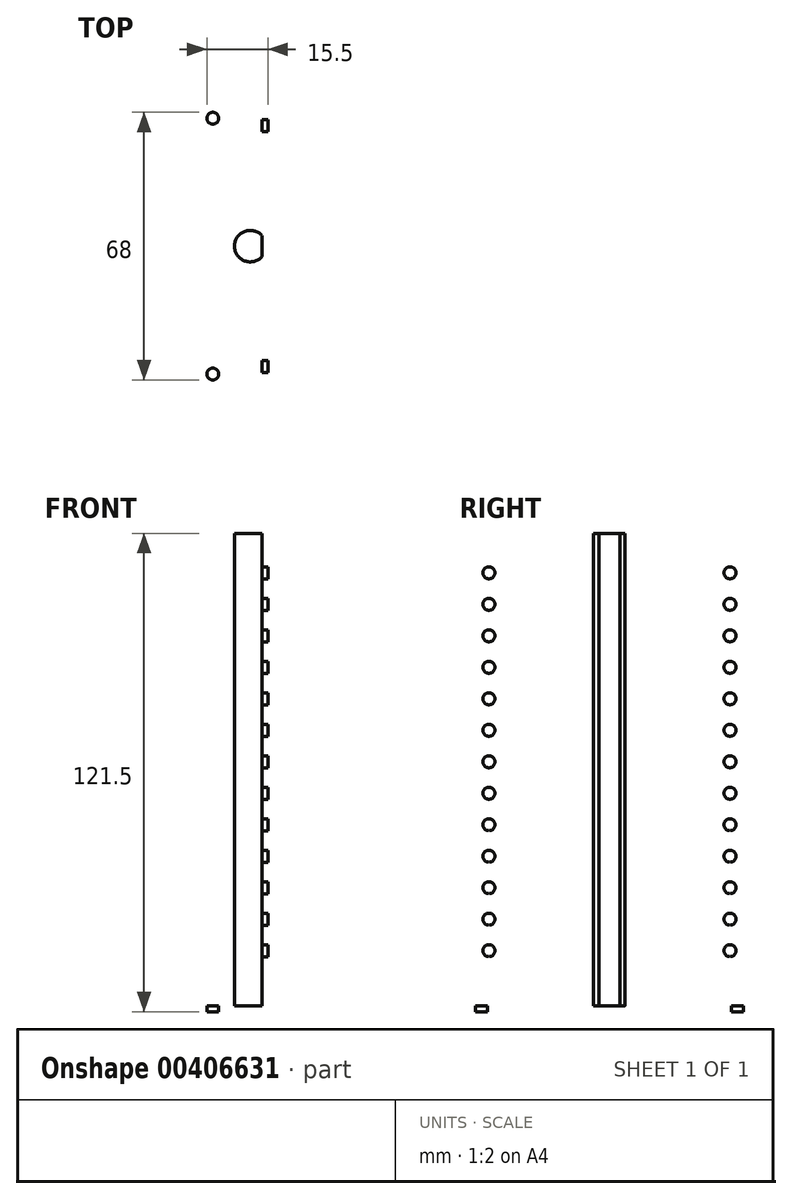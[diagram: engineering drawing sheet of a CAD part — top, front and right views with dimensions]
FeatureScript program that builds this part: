
annotation { "Feature Type Name" : "Feature", "Feature Type Description" : "" }
export const myFeature = defineFeature(function(context is Context, id is Id, definition is map)
    precondition{}
    {
        {
            var Q0;
            Q0=qCreatedBy(makeId("Top.planeOp"),FACE);
            var sketch = newSketch(context, id + "F0", { "sketchPlane" : qUnion([Q0])});
            skLineSegment(sketch, "E0.bottom", {"start": v(12.5, -37.5) * mm, "end": v(-12.5, -37.5) * mm});
            skLineSegment(sketch, "E0.top", {"start": v(12.5, 37.5) * mm, "end": v(-12.5, 37.5) * mm});
            skLineSegment(sketch, "E0.left", {"start": v(12.5, -37.5) * mm, "end": v(12.5, 37.5) * mm});
            skLineSegment(sketch, "E0.right", {"start": v(-12.5, -37.5) * mm, "end": v(-12.5, 37.5) * mm});
            skPoint(sketch, "E0.middle", {"position": v(0, 0) * mm});
            skSolve(sketch);
        }
        {
            var Q0;
            Q0=makeQuery(id+"F0.imprint","IMPRINT",FACE,{"disambiguationData":[TD([[makeQuery(id+"F0.imprint","IMPRINT",EDGE,{"derivedFrom":sQuery(id+"F0.wireOp",EDGE,"E0.bottom")}),-1.0]])]});
            extrude(context, id + "F1", {"entities" : qUnion([Q0]), "depth" : 120 * mm});
        }
        {
            var Q0;
            Q0=makeQuery(id+"F1.opExtrude","SWEPT_FACE",FACE,{"disambiguationData":[OSD([sQuery(id+"F0.wireOp",EDGE,"E0.left")])]});
            var sketch = newSketch(context, id + "F2", { "sketchPlane" : qUnion([Q0])});
            skLineSegment(sketch, "E1", {"start": v(0, 120) * mm, "end": v(0, 0) * mm, "construction": true});
            skLineSegment(sketch, "E2.0", {"start": v(-30.62, 120) * mm, "end": v(-30.61, 0) * mm, "construction": true});
            skLineSegment(sketch, "E3.0", {"start": v(30.61, 120) * mm, "end": v(30.61, 0) * mm, "construction": true});
            skLineSegment(sketch, "E4", {"start": v(-37.5, 110) * mm, "end": v(37.5, 110) * mm, "construction": true});
            skLineSegment(sketch, "E5.0", {"start": v(-37.5, 102) * mm, "end": v(37.5, 102) * mm, "construction": true});
            skLineSegment(sketch, "E6.0", {"start": v(-37.5, 94) * mm, "end": v(37.5, 94) * mm, "construction": true});
            skLineSegment(sketch, "E7.0", {"start": v(-37.5, 86) * mm, "end": v(37.5, 86) * mm, "construction": true});
            skLineSegment(sketch, "E8.0", {"start": v(-37.5, 78) * mm, "end": v(37.5, 78) * mm, "construction": true});
            skLineSegment(sketch, "E9.0", {"start": v(-37.5, 70) * mm, "end": v(37.5, 70) * mm, "construction": true});
            skLineSegment(sketch, "E10.0", {"start": v(-37.5, 62) * mm, "end": v(37.5, 62) * mm, "construction": true});
            skLineSegment(sketch, "E11.0", {"start": v(-37.5, 54) * mm, "end": v(37.5, 54) * mm, "construction": true});
            skLineSegment(sketch, "E12.0", {"start": v(-37.5, 46) * mm, "end": v(37.5, 46) * mm, "construction": true});
            skLineSegment(sketch, "E13.0", {"start": v(-37.5, 38) * mm, "end": v(37.5, 38) * mm, "construction": true});
            skLineSegment(sketch, "E14.0", {"start": v(-37.5, 30) * mm, "end": v(37.5, 30) * mm, "construction": true});
            skLineSegment(sketch, "E15.0", {"start": v(-37.5, 22) * mm, "end": v(37.5, 22) * mm, "construction": true});
            skLineSegment(sketch, "E16.0", {"start": v(-37.5, 14) * mm, "end": v(37.5, 14) * mm, "construction": true});
            skCircle(sketch, "E17", {"center": v(-30.62, 110) * mm, "radius": 1.52 * mm});
            skCircle(sketch, "E18", {"center": v(-30.62, 102) * mm, "radius": 1.52 * mm});
            skCircle(sketch, "E19", {"center": v(-30.62, 94) * mm, "radius": 1.52 * mm});
            skCircle(sketch, "E20", {"center": v(-30.62, 86) * mm, "radius": 1.52 * mm});
            skCircle(sketch, "E21", {"center": v(-30.62, 78) * mm, "radius": 1.52 * mm});
            skCircle(sketch, "E22", {"center": v(-30.62, 70) * mm, "radius": 1.52 * mm});
            skCircle(sketch, "E23", {"center": v(-30.62, 62) * mm, "radius": 1.52 * mm});
            skCircle(sketch, "E24", {"center": v(-30.62, 54) * mm, "radius": 1.52 * mm});
            skCircle(sketch, "E25", {"center": v(-30.62, 46) * mm, "radius": 1.52 * mm});
            skCircle(sketch, "E26", {"center": v(-30.61, 30) * mm, "radius": 1.52 * mm});
            skCircle(sketch, "E27", {"center": v(-30.62, 38) * mm, "radius": 1.52 * mm});
            skCircle(sketch, "E28", {"center": v(-30.62, 22) * mm, "radius": 1.52 * mm});
            skCircle(sketch, "E29", {"center": v(-30.61, 14) * mm, "radius": 1.52 * mm});
            skCircle(sketch, "E30.MirrorC", {"center": v(30.61, 110) * mm, "radius": 1.52 * mm});
            skCircle(sketch, "E31.MirrorC", {"center": v(30.61, 102) * mm, "radius": 1.52 * mm});
            skCircle(sketch, "E32.MirrorC", {"center": v(30.61, 94) * mm, "radius": 1.52 * mm});
            skCircle(sketch, "E33.MirrorC", {"center": v(30.61, 86) * mm, "radius": 1.52 * mm});
            skCircle(sketch, "E34.MirrorC", {"center": v(30.61, 78) * mm, "radius": 1.52 * mm});
            skCircle(sketch, "E35.MirrorC", {"center": v(30.61, 70) * mm, "radius": 1.52 * mm});
            skCircle(sketch, "E36.MirrorC", {"center": v(30.61, 62) * mm, "radius": 1.52 * mm});
            skCircle(sketch, "E37.MirrorC", {"center": v(30.61, 54) * mm, "radius": 1.52 * mm});
            skCircle(sketch, "E38.MirrorC", {"center": v(30.61, 46) * mm, "radius": 1.52 * mm});
            skCircle(sketch, "E39.MirrorC", {"center": v(30.61, 38) * mm, "radius": 1.52 * mm});
            skCircle(sketch, "E40.MirrorC", {"center": v(30.61, 30) * mm, "radius": 1.52 * mm});
            skCircle(sketch, "E41.MirrorC", {"center": v(30.61, 22) * mm, "radius": 1.52 * mm});
            skCircle(sketch, "E42.MirrorC", {"center": v(30.61, 14) * mm, "radius": 1.52 * mm});
            skSolve(sketch);
        }
        {
            var Q0;
            Q0 = qSketchRegion(id + "F2", true);
            extrude(context, id + "F3", {"entities" : qUnion([Q0]), "operationType" : NewBodyOperationType.ADD, "depth" : 1.5 * mm});
        }
        {
            var Q0;
            Q0=makeQuery(id+"F1.opExtrude","CAP_FACE",FACE,{"disambiguationData":[OSD([sQuery(id+"F0.wireOp",EDGE,"E0.bottom"),sQuery(id+"F0.wireOp",EDGE,"E0.top"),sQuery(id+"F0.wireOp",EDGE,"E0.left"),sQuery(id+"F0.wireOp",EDGE,"E0.right")])],"isStart":false});
            var sketch = newSketch(context, id + "F4", { "sketchPlane" : qUnion([Q0])});
            skArc(sketch, "E43", {"start": v(12.5, -2.65) * mm, "mid": v(5.5, 0) * mm, "end": v(12.5, 2.65) * mm});
            skSolve(sketch);
        }
        {
            var Q0;
            Q0 = qSketchRegion(id + "F4", true);
            var Q1;
            {var subQ0=sQuery(id+"F4.wireOp",EDGE,"E43");Q1=makeQuery(id+"F4.imprint","IMPRINT",FACE,{"disambiguationData":[TD([[makeQuery(id+"F4.imprint","IMPRINT",EDGE,{"derivedFrom":subQ0}),-1.0]])]});}
            extrude(context, id + "F5", {"entities" : qUnion([Q0, Q1]), "operationType" : NewBodyOperationType.REMOVE, "endBound" : BoundingType.THROUGH_ALL, "oppositeDirection" : true, "depth" : 25 * mm});
        }
        {
            var Q0;
            Q0=makeQuery(id+"F1.opExtrude","CAP_FACE",FACE,{"disambiguationData":[OSD([sQuery(id+"F0.wireOp",EDGE,"E0.bottom"),sQuery(id+"F0.wireOp",EDGE,"E0.top"),sQuery(id+"F0.wireOp",EDGE,"E0.left"),sQuery(id+"F0.wireOp",EDGE,"E0.right")])],"isStart":true});
            var sketch = newSketch(context, id + "F6", { "sketchPlane" : qUnion([Q0])});
            skCircle(sketch, "E44", {"center": v(0, 32.5) * mm, "radius": 1.5 * mm});
            skCircle(sketch, "E45", {"center": v(0, -32.5) * mm, "radius": 1.5 * mm});
            skSolve(sketch);
        }
        {
            var Q0;
            Q0 = qSketchRegion(id + "F6", true);
            extrude(context, id + "F7", {"entities" : qUnion([Q0]), "operationType" : NewBodyOperationType.ADD, "depth" : 1.5 * mm});
        }
    });
